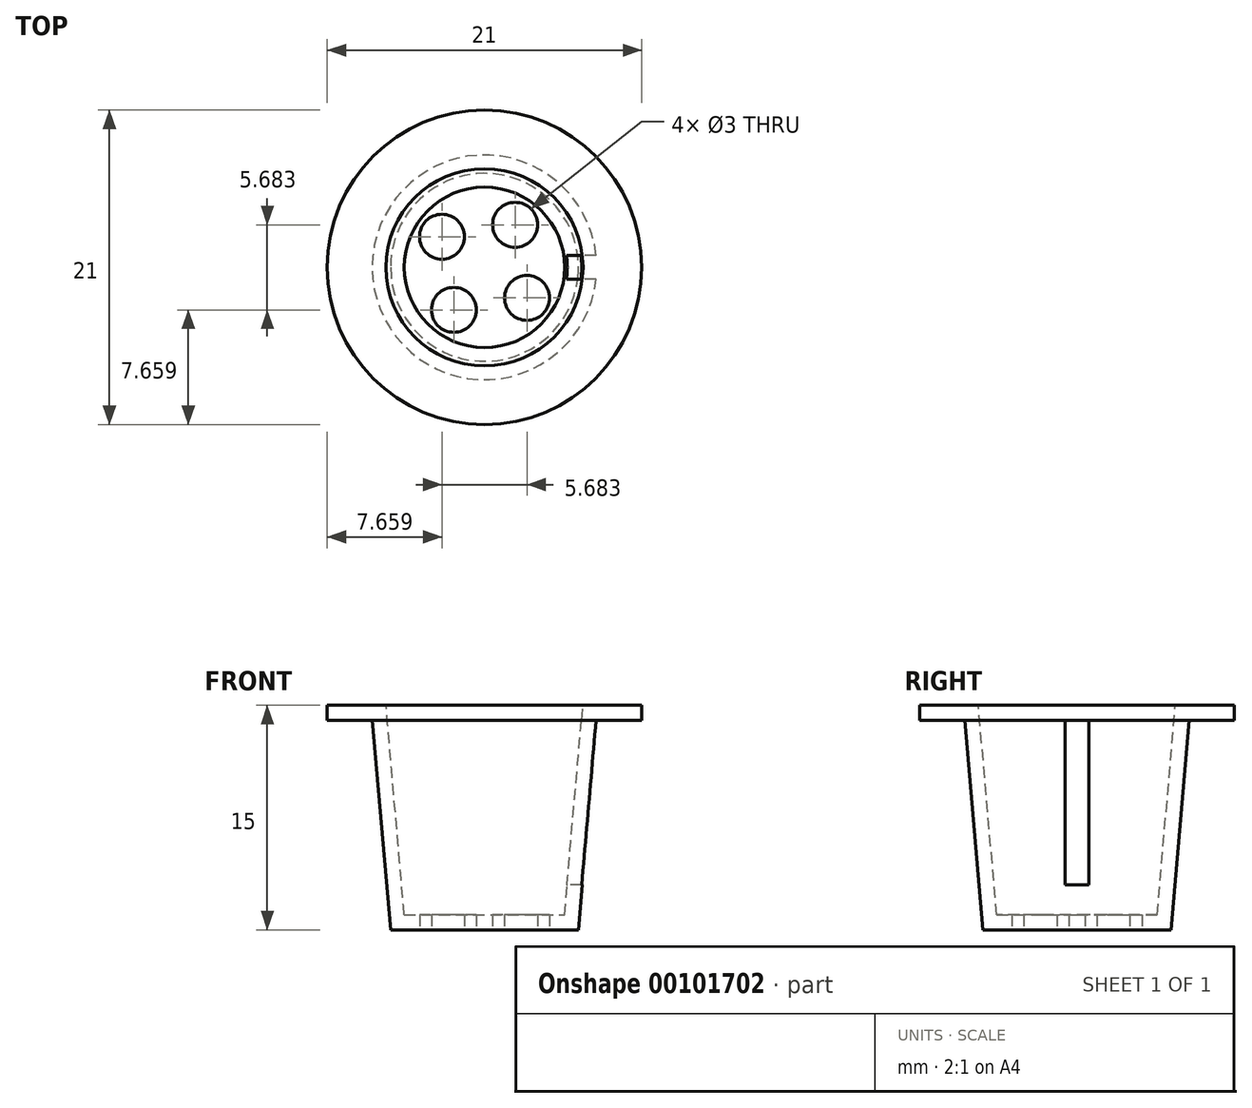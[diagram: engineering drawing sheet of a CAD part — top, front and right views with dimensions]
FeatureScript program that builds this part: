
annotation { "Feature Type Name" : "Feature", "Feature Type Description" : "" }
export const myFeature = defineFeature(function(context is Context, id is Id, definition is map)
    precondition{}
    {
        {
            var Q0;
            Q0=qCreatedBy(makeId("Front.planeOp"),FACE);
            var sketch = newSketch(context, id + "F0", { "sketchPlane" : qUnion([Q0])});
            skLineSegment(sketch, "E0", {"start": v(10.5, 14) * mm, "end": v(7.5, 14) * mm});
            skLineSegment(sketch, "E1", {"start": v(7.5, 14) * mm, "end": v(6.28, 0) * mm});
            skLineSegment(sketch, "E2", {"start": v(6.28, 0) * mm, "end": v(0, 0) * mm});
            skLineSegment(sketch, "E3.0", {"start": v(5.36, 1) * mm, "end": v(0, 1) * mm});
            skLineSegment(sketch, "E3.1", {"start": v(6.58, 15) * mm, "end": v(5.36, 1) * mm});
            skLineSegment(sketch, "E3.2", {"start": v(10.5, 15) * mm, "end": v(6.58, 15) * mm});
            skLineSegment(sketch, "E4", {"start": v(0, 0) * mm, "end": v(0, 1) * mm});
            skLineSegment(sketch, "E5", {"start": v(10.5, 14) * mm, "end": v(10.5, 15) * mm});
            skSolve(sketch);
        }
        {
            var Q0;
            Q0=makeQuery(id+"F0.imprint","IMPRINT",FACE,{"disambiguationData":[TD([[makeQuery(id+"F0.imprint","IMPRINT",EDGE,{"derivedFrom":sQuery(id+"F0.wireOp",EDGE,"E0")}),-1.0]])]});
            var Q1;
            Q1=sQuery(id+"F0.wireOp",EDGE,"E4");
            revolve(context, id + "F1", {"entities" : qUnion([Q0]), "axis" : qUnion([Q1]), "revolveType" : RevolveType.FULL});
        }
        {
            var Q0;
            Q0=qCreatedBy(makeId("Right.planeOp"),FACE);
            var sketch = newSketch(context, id + "F2", { "sketchPlane" : qUnion([Q0])});
            skLineSegment(sketch, "E6.bottom", {"start": v(-0.8, 14) * mm, "end": v(0.8, 14) * mm});
            skLineSegment(sketch, "E6.left", {"start": v(-0.8, 14) * mm, "end": v(-0.8, 0) * mm});
            skLineSegment(sketch, "E6.right", {"start": v(0.8, 14) * mm, "end": v(0.8, 0) * mm});
            skPoint(sketch, "E6.middle", {"position": v(0, 7) * mm});
            skLineSegment(sketch, "E7", {"start": v(-0.8, 3) * mm, "end": v(0.8, 3) * mm});
            skSolve(sketch);
        }
        {
            var Q0;
            Q0=makeQuery(id+"F2.imprint","IMPRINT",FACE,{"disambiguationData":[TD([[makeQuery(id+"F2.imprint","IMPRINT",EDGE,{"derivedFrom":sQuery(id+"F2.wireOp",EDGE,"E6.bottom")}),-1.0]])]});
            extrude(context, id + "F3", {"entities" : qUnion([Q0]), "operationType" : NewBodyOperationType.REMOVE, "endBound" : BoundingType.THROUGH_ALL, "depth" : 25 * mm});
        }
        {
            var Q0;
            Q0=makeQuery(id+"F1.opRevolve","SWEPT_FACE",FACE,{"disambiguationData":[OSD([sQuery(id+"F0.wireOp",EDGE,"E2")])]});
            var sketch = newSketch(context, id + "F4", { "sketchPlane" : qUnion([Q0])});
            skCircle(sketch, "E8", {"center": v(2.84, 2.04) * mm, "radius": 1.5 * mm});
            skCircle(sketch, "E9.1.0", {"center": v(-2.04, 2.84) * mm, "radius": 1.5 * mm});
            skCircle(sketch, "E9.2.0", {"center": v(-2.84, -2.04) * mm, "radius": 1.5 * mm});
            skCircle(sketch, "E9.3.0", {"center": v(2.04, -2.84) * mm, "radius": 1.5 * mm});
            skPoint(sketch, "E9.center", {"position": v(0, 0) * mm});
            skSolve(sketch);
        }
        {
            var Q0;
            Q0=makeQuery(id+"F4.imprint","IMPRINT",FACE,{"disambiguationData":[TD([[makeQuery(id+"F4.imprint","IMPRINT",EDGE,{"derivedFrom":sQuery(id+"F4.wireOp",EDGE,"E9.2.0")}),1.0]])]});
            var Q1;
            Q1=makeQuery(id+"F4.imprint","IMPRINT",FACE,{"disambiguationData":[TD([[makeQuery(id+"F4.imprint","IMPRINT",EDGE,{"derivedFrom":sQuery(id+"F4.wireOp",EDGE,"E9.1.0")}),1.0]])]});
            var Q2;
            Q2=makeQuery(id+"F4.imprint","IMPRINT",FACE,{"disambiguationData":[TD([[makeQuery(id+"F4.imprint","IMPRINT",EDGE,{"derivedFrom":sQuery(id+"F4.wireOp",EDGE,"E8")}),1.0]])]});
            var Q3;
            Q3=makeQuery(id+"F4.imprint","IMPRINT",FACE,{"disambiguationData":[TD([[makeQuery(id+"F4.imprint","IMPRINT",EDGE,{"derivedFrom":sQuery(id+"F4.wireOp",EDGE,"E9.3.0")}),1.0]])]});
            extrude(context, id + "F5", {"entities" : qUnion([Q0, Q1, Q2, Q3]), "operationType" : NewBodyOperationType.REMOVE, "oppositeDirection" : true, "depth" : 25 * mm});
        }
    });
